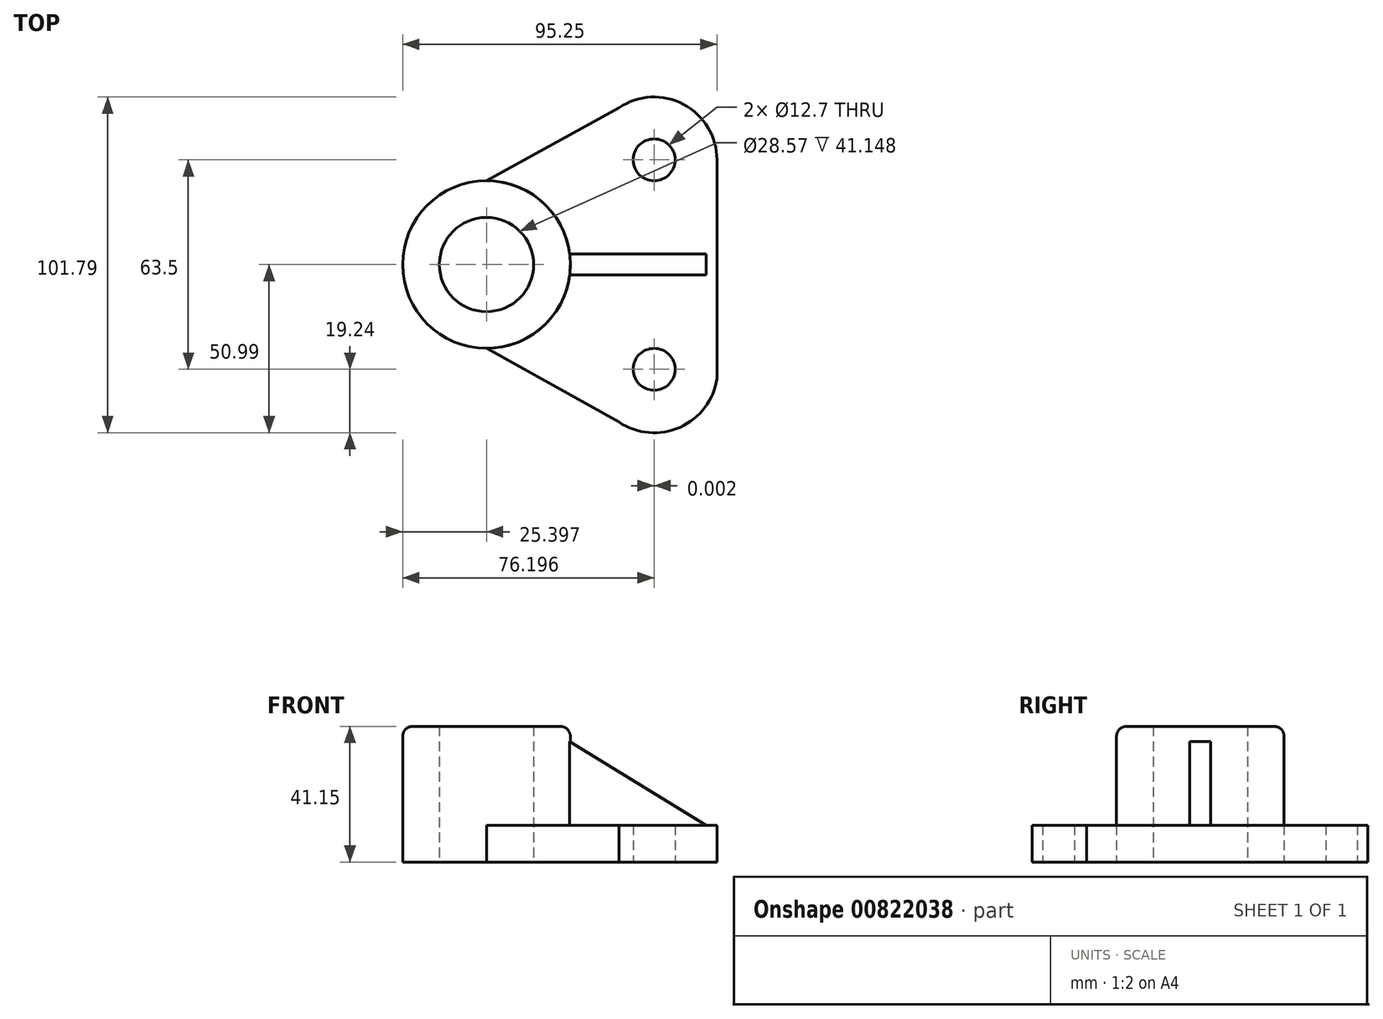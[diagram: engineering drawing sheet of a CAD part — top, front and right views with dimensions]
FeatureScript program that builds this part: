
annotation { "Feature Type Name" : "Feature", "Feature Type Description" : "" }
export const myFeature = defineFeature(function(context is Context, id is Id, definition is map)
    precondition{}
    {
        {
            var Q0;
            Q0=qCreatedBy(makeId("Top.planeOp"),FACE);
            var sketch = newSketch(context, id + "F0", { "sketchPlane" : qUnion([Q0])});
            skCircle(sketch, "E0", {"center": v(-32.08, 29.62) * mm, "radius": 25.4 * mm});
            skCircle(sketch, "E1", {"center": v(-32.08, 29.62) * mm, "radius": 14.29 * mm});
            skLineSegment(sketch, "E2", {"start": v(-32.08, 55.02) * mm, "end": v(8.06, 77.16) * mm});
            skLineSegment(sketch, "E3", {"start": v(-32.08, 4.22) * mm, "end": v(8.06, -18.14) * mm});
            skArc(sketch, "E4", {"start": v(8.06, -18.14) * mm, "mid": v(26.59, -19.68) * mm, "end": v(37.77, -4.83) * mm});
            skCircle(sketch, "E5", {"center": v(18.72, -2.13) * mm, "radius": 6.35 * mm});
            skLineSegment(sketch, "E6", {"start": v(37.77, -4.83) * mm, "end": v(37.77, 61.37) * mm});
            skArc(sketch, "E7", {"start": v(37.77, 61.37) * mm, "mid": v(27.66, 78.2) * mm, "end": v(8.06, 77.16) * mm});
            skCircle(sketch, "E8", {"center": v(18.72, 61.37) * mm, "radius": 6.35 * mm});
            skLineSegment(sketch, "E9", {"start": v(-75.3, 29.62) * mm, "end": v(64.76, 29.62) * mm, "construction": true});
            skSolve(sketch);
        }
        {
            var Q0;
            Q0=makeQuery(id+"F0.imprint","IMPRINT",FACE,{"disambiguationData":[TD([[makeQuery(id+"F0.imprint","IMPRINT",EDGE,{"derivedFrom":sQuery(id+"F0.wireOp",EDGE,"E1")}),-1.0]])]});
            extrude(context, id + "F1", {"entities" : qUnion([Q0]), "depth" : 41.15 * mm, "offsetDistance" : 25.4 * mm});
        }
        {
            var Q0;
            {var subQ1=sQuery(id+"F0.wireOp",EDGE,"E2");Q0=makeQuery(id+"F0.imprint","IMPRINT",FACE,{"disambiguationData":[TD([[makeQuery(id+"F0.imprint","IMPRINT",EDGE,{"derivedFrom":subQ1}),-1.0]])]});}
            extrude(context, id + "F2", {"entities" : qUnion([Q0]), "operationType" : NewBodyOperationType.ADD, "depth" : 11.18 * mm, "offsetDistance" : 25.4 * mm});
        }
        {
            var Q0;
            Q0=makeQuery(id+"F1.opExtrude","CAP_EDGE",EDGE,{"disambiguationData":[OSD([sQuery(id+"F0.wireOp",EDGE,"E0")])],"isStart":false});
            fillet(context, id + "F3", {"entities" : qUnion([Q0]), "radius" : 3.05 * mm, "tangentPropagation" : true, "allowEdgeOverflow" : false});
        }
        {
            var Q0;
            Q0=makeQuery(id+"F2.opExtrude","CAP_FACE",FACE,{"disambiguationData":[OSD([sQuery(id+"F0.wireOp",EDGE,"E0"),sQuery(id+"F0.wireOp",EDGE,"E2"),sQuery(id+"F0.wireOp",EDGE,"E3"),sQuery(id+"F0.wireOp",EDGE,"E4"),sQuery(id+"F0.wireOp",EDGE,"E5"),sQuery(id+"F0.wireOp",EDGE,"E6"),sQuery(id+"F0.wireOp",EDGE,"E7"),sQuery(id+"F0.wireOp",EDGE,"E8")])],"isStart":false});
            var sketch = newSketch(context, id + "F4", { "sketchPlane" : qUnion([Q0])});
            skLineSegment(sketch, "E10", {"start": v(37.77, 29.74) * mm, "end": v(37.77, 32.8) * mm});
            skLineSegment(sketch, "E11", {"start": v(37.77, 32.8) * mm, "end": v(-6.88, 32.8) * mm});
            skLineSegment(sketch, "E12", {"start": v(37.77, 29.74) * mm, "end": v(37.77, 26.45) * mm});
            skLineSegment(sketch, "E13", {"start": v(37.77, 26.45) * mm, "end": v(-6.88, 26.45) * mm});
            skLineSegment(sketch, "E14", {"start": v(34.46, 32.8) * mm, "end": v(34.46, 26.45) * mm});
            skSolve(sketch);
        }
        {
            var Q0;
            {var subQ3=sQuery(id+"F4.wireOp",EDGE,"E14");Q0=makeQuery(id+"F4.imprint","IMPRINT",FACE,{"disambiguationData":[TD([[makeQuery(id+"F4.imprint","IMPRINT",EDGE,{"derivedFrom":subQ3}),-1.0]])]});}
            extrude(context, id + "F5", {"entities" : qUnion([Q0]), "operationType" : NewBodyOperationType.ADD, "depth" : 25.4 * mm, "offsetDistance" : 25.4 * mm});
        }
        {
            var Q0;
            Q0=makeQuery(id+"F5.opExtrude","SWEPT_FACE",FACE,{"disambiguationData":[OSD([sQuery(id+"F4.wireOp",EDGE,"E11")])]});
            var sketch = newSketch(context, id + "F6", { "sketchPlane" : qUnion([Q0])});
            skLineSegment(sketch, "E15", {"start": v(6.88, 36.58) * mm, "end": v(-34.46, 11.18) * mm});
            skSolve(sketch);
        }
        {
            var Q0;
            Q0=makeQuery(id+"F6.imprint","IMPRINT",FACE,{"disambiguationData":[TD([[makeQuery(id+"F6.imprint","IMPRINT",EDGE,{"derivedFrom":sQuery(id+"F6.wireOp",EDGE,"E15")}),-1.0]])]});
            extrude(context, id + "F7", {"entities" : qUnion([Q0]), "operationType" : NewBodyOperationType.REMOVE, "endBound" : BoundingType.THROUGH_ALL, "oppositeDirection" : true, "depth" : 25.4 * mm, "offsetDistance" : 25.4 * mm});
        }
    });
